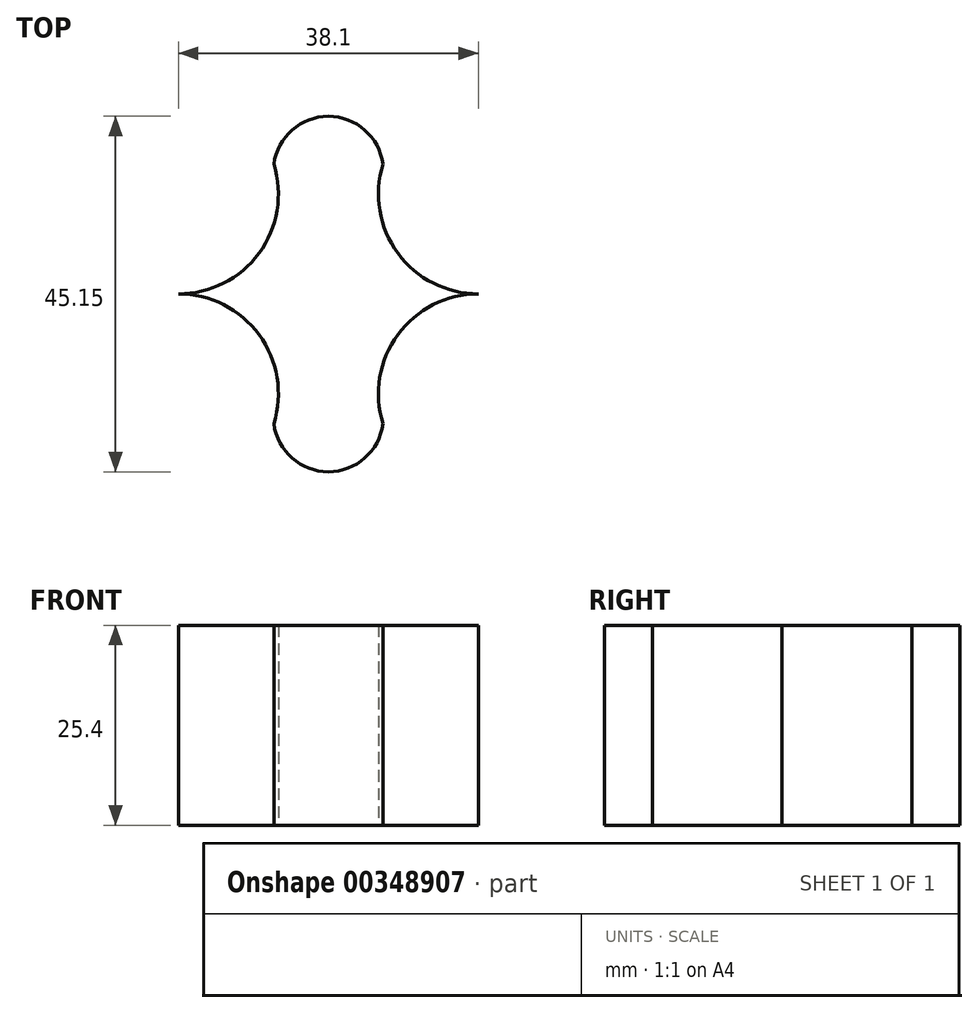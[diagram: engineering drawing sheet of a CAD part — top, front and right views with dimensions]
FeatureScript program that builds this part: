
annotation { "Feature Type Name" : "Feature", "Feature Type Description" : "" }
export const myFeature = defineFeature(function(context is Context, id is Id, definition is map)
    precondition{}
    {
        {
            var Q0;
            Q0=qCreatedBy(makeId("Top.planeOp"),FACE);
            var sketch = newSketch(context, id + "F0", { "sketchPlane" : qUnion([Q0])});
            skLineSegment(sketch, "E0.bottom", {"start": v(-19.05, 12.7) * mm, "end": v(19.05, 12.7) * mm});
            skLineSegment(sketch, "E0.top", {"start": v(-19.05, -12.7) * mm, "end": v(19.05, -12.7) * mm});
            skLineSegment(sketch, "E0.left", {"start": v(-19.05, 12.7) * mm, "end": v(-19.05, -12.7) * mm});
            skLineSegment(sketch, "E0.right", {"start": v(19.05, 12.7) * mm, "end": v(19.05, -12.7) * mm});
            skPoint(sketch, "E0.middle", {"position": v(0, 0) * mm});
            skCircle(sketch, "E1", {"center": v(-19.05, 12.7) * mm, "radius": 12.7 * mm});
            skCircle(sketch, "E2", {"center": v(19.05, 12.7) * mm, "radius": 12.7 * mm});
            skCircle(sketch, "E3", {"center": v(19.05, -12.7) * mm, "radius": 12.7 * mm});
            skCircle(sketch, "E4", {"center": v(-19.05, -12.7) * mm, "radius": 12.7 * mm});
            skArc(sketch, "E5", {"start": v(6.35, 12.7) * mm, "mid": v(0, 22.56) * mm, "end": v(-6.35, 12.7) * mm});
            skArc(sketch, "E6", {"start": v(-6.35, -12.7) * mm, "mid": v(0, -22.6) * mm, "end": v(6.35, -12.7) * mm});
            skSolve(sketch);
        }
        {
            var Q0;
            {var subQ1=sQuery(id+"F0.wireOp",EDGE,"E0.bottom");var subQ5=sQuery(id+"F0.wireOp",EDGE,"E1");var subQ6=makeQuery(id+"F0.imprint","INTERSECT",VERTEX,{"derivedFrom":[subQ1,subQ5]});Q0=makeQuery(id+"F0.imprint","IMPRINT",FACE,{"disambiguationData":[TD([[makeQuery(id+"F0.imprint","IMPRINT",EDGE,{"disambiguationData":[TD([[subQ6,-1.0]])],"derivedFrom":subQ1}),-1.0]])]});}
            var Q1;
            {var subQ0=sQuery(id+"F0.wireOp",EDGE,"E6");var subQ4=sQuery(id+"F0.wireOp",EDGE,"E3");var subQ6=makeQuery(id+"F0.imprint","INTERSECT",VERTEX,{"derivedFrom":[subQ4,subQ0]});Q1=makeQuery(id+"F0.imprint","IMPRINT",FACE,{"disambiguationData":[TD([[makeQuery(id+"F0.imprint","IMPRINT",EDGE,{"disambiguationData":[TD([[subQ6,1.0]])],"derivedFrom":subQ0}),1.0]])]});}
            var Q2;
            {var subQ0=sQuery(id+"F0.wireOp",EDGE,"E5");var subQ4=sQuery(id+"F0.wireOp",EDGE,"E1");var subQ6=makeQuery(id+"F0.imprint","INTERSECT",VERTEX,{"derivedFrom":[subQ4,subQ0]});Q2=makeQuery(id+"F0.imprint","IMPRINT",FACE,{"disambiguationData":[TD([[makeQuery(id+"F0.imprint","IMPRINT",EDGE,{"disambiguationData":[TD([[subQ6,1.0]])],"derivedFrom":subQ0}),1.0]])]});}
            var Q3;
            {var subQ0=sQuery(id+"F0.wireOp",EDGE,"umDyHlC7-vyf4-b1re-Do4E-5G1J2xMohJVg");Q3=makeQuery(id+"F0.imprint","IMPRINT",FACE,{"disambiguationData":[TD([[makeQuery(id+"F0.imprint","IMPRINT",EDGE,{"derivedFrom":subQ0}),-1.0]])]});}
            extrude(context, id + "F1", {"entities" : qUnion([Q0, Q1, Q2, Q3]), "depth" : 25.4 * mm});
        }
    });
